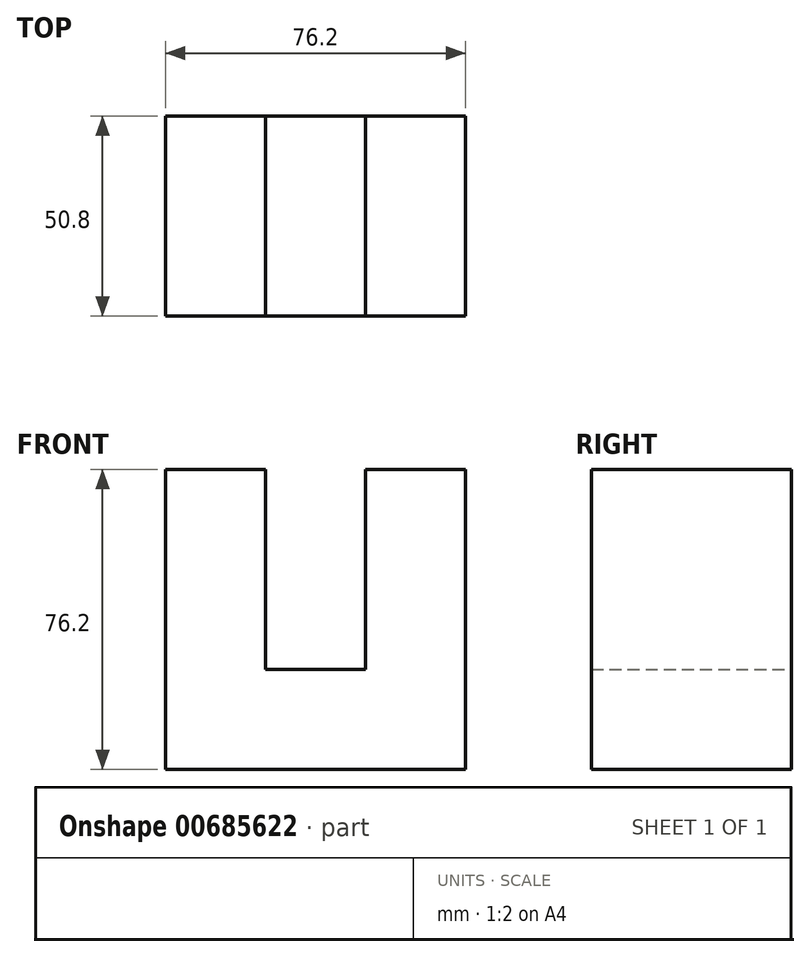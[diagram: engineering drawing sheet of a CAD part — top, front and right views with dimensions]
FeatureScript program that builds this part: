
annotation { "Feature Type Name" : "Feature", "Feature Type Description" : "" }
export const myFeature = defineFeature(function(context is Context, id is Id, definition is map)
    precondition{}
    {
        {
            var Q0;
            Q0=qCreatedBy(makeId("Front.planeOp"),FACE);
            var sketch = newSketch(context, id + "F0", { "sketchPlane" : qUnion([Q0])});
            skLineSegment(sketch, "E0", {"start": v(-76.17, 76.2) * mm, "end": v(-76.17, 0) * mm});
            skLineSegment(sketch, "E1", {"start": v(-76.17, 0) * mm, "end": v(0.03, 0) * mm});
            skLineSegment(sketch, "E2", {"start": v(0.03, 0) * mm, "end": v(0.03, 76.2) * mm});
            skLineSegment(sketch, "E3", {"start": v(-76.17, 76.2) * mm, "end": v(-50.77, 76.2) * mm});
            skLineSegment(sketch, "E4", {"start": v(-50.77, 76.2) * mm, "end": v(-50.77, 25.4) * mm});
            skLineSegment(sketch, "E5", {"start": v(-50.77, 25.4) * mm, "end": v(-25.37, 25.4) * mm});
            skLineSegment(sketch, "E6", {"start": v(-25.37, 25.4) * mm, "end": v(-25.37, 76.2) * mm});
            skLineSegment(sketch, "E7", {"start": v(-25.37, 76.2) * mm, "end": v(0.03, 76.2) * mm});
            skSolve(sketch);
        }
        {
            var Q0;
            Q0=makeQuery(id+"F0.imprint","IMPRINT",FACE,{"disambiguationData":[TD([[makeQuery(id+"F0.imprint","IMPRINT",EDGE,{"derivedFrom":sQuery(id+"F0.wireOp",EDGE,"E0")}),1.0]])]});
            extrude(context, id + "F1", {"entities" : qUnion([Q0]), "depth" : 50.8 * mm, "offsetDistance" : 25.4 * mm});
        }
    });
